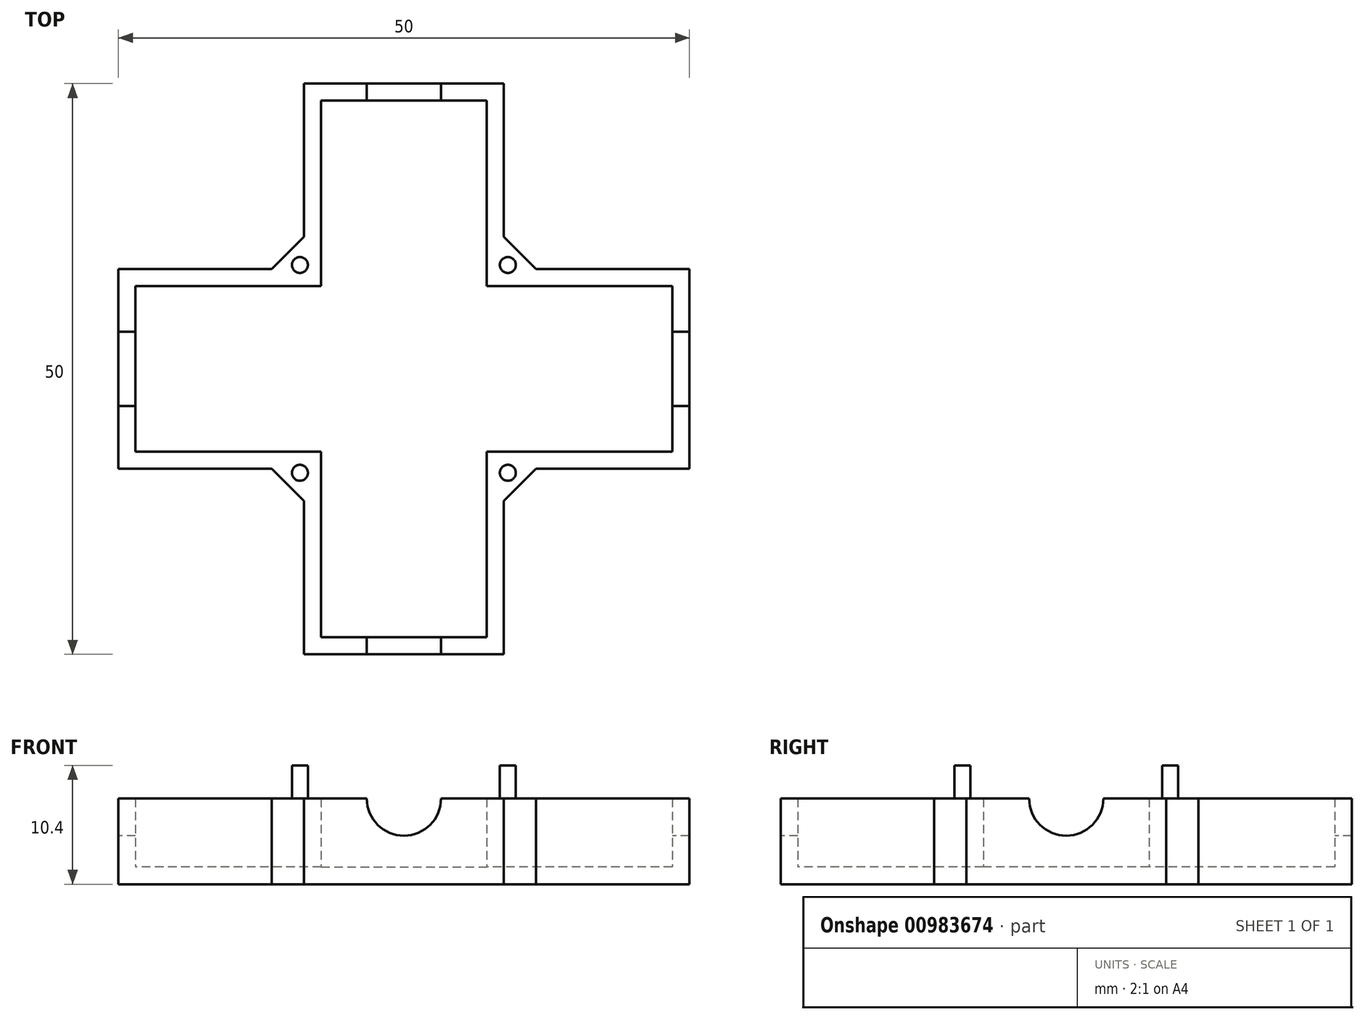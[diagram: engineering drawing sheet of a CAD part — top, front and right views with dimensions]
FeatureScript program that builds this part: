
annotation { "Feature Type Name" : "Feature", "Feature Type Description" : "" }
export const myFeature = defineFeature(function(context is Context, id is Id, definition is map)
    precondition{}
    {
        {
            var Q0;
            Q0=qCreatedBy(makeId("Top.planeOp"),FACE);
            var sketch = newSketch(context, id + "F0", { "sketchPlane" : qUnion([Q0])});
            skLineSegment(sketch, "E0.bottom", {"start": v(25, 8.75) * mm, "end": v(8.75, 8.75) * mm});
            skLineSegment(sketch, "E0.top", {"start": v(25, -8.75) * mm, "end": v(8.75, -8.75) * mm});
            skLineSegment(sketch, "E0.left", {"start": v(25, 8.75) * mm, "end": v(25, -8.75) * mm});
            skLineSegment(sketch, "E0.right", {"start": v(-25, 8.75) * mm, "end": v(-25, -8.75) * mm});
            skPoint(sketch, "E0.middle", {"position": v(0, 0) * mm});
            skLineSegment(sketch, "E1.bottom", {"start": v(-8.75, 25) * mm, "end": v(8.75, 25) * mm});
            skLineSegment(sketch, "E1.top", {"start": v(-8.75, -25) * mm, "end": v(8.75, -25) * mm});
            skLineSegment(sketch, "E1.left", {"start": v(-8.75, 25) * mm, "end": v(-8.75, 8.75) * mm});
            skLineSegment(sketch, "E1.right", {"start": v(8.75, 25) * mm, "end": v(8.75, 8.75) * mm});
            skLineSegment(sketch, "E2.trimOffspring", {"start": v(-8.75, 8.75) * mm, "end": v(-25, 8.75) * mm});
            skLineSegment(sketch, "E3.trimOffspring", {"start": v(-8.75, -8.75) * mm, "end": v(-8.75, -25) * mm});
            skLineSegment(sketch, "E4.trimOffspring", {"start": v(-8.75, -8.75) * mm, "end": v(-25, -8.75) * mm});
            skLineSegment(sketch, "E5.trimOffspring", {"start": v(8.75, -8.75) * mm, "end": v(8.75, -25) * mm});
            skSolve(sketch);
        }
        {
            var Q0;
            Q0=qSketchRegion(id+"F0",true);
            extrude(context, id + "F1", {"entities" : qUnion([Q0]), "depth" : 7.5 * mm, "offsetDistance" : 25 * mm});
        }
        {
            var Q0;
            Q0=makeQuery(id+"F1.opExtrude","CAP_FACE",FACE,{"disambiguationData":[OSD([sQuery(id+"F0.wireOp",EDGE,"E0.bottom"),sQuery(id+"F0.wireOp",EDGE,"E0.top"),sQuery(id+"F0.wireOp",EDGE,"E0.left"),sQuery(id+"F0.wireOp",EDGE,"E0.right"),sQuery(id+"F0.wireOp",EDGE,"E1.bottom"),sQuery(id+"F0.wireOp",EDGE,"E1.top"),sQuery(id+"F0.wireOp",EDGE,"E1.left"),sQuery(id+"F0.wireOp",EDGE,"E1.right"),sQuery(id+"F0.wireOp",EDGE,"E2.trimOffspring"),sQuery(id+"F0.wireOp",EDGE,"E3.trimOffspring"),sQuery(id+"F0.wireOp",EDGE,"E4.trimOffspring"),sQuery(id+"F0.wireOp",EDGE,"E5.trimOffspring")])],"isStart":false});
            shell(context, id + "F2", {"entities" : qUnion([Q0]), "thickness" : 1.5 * mm});
        }
        {
            var Q0;
            Q0=makeQuery(id+"F1.opExtrude","CAP_FACE",FACE,{"disambiguationData":[OSD([sQuery(id+"F0.wireOp",EDGE,"E0.bottom"),sQuery(id+"F0.wireOp",EDGE,"E0.top"),sQuery(id+"F0.wireOp",EDGE,"E0.left"),sQuery(id+"F0.wireOp",EDGE,"E0.right"),sQuery(id+"F0.wireOp",EDGE,"E1.bottom"),sQuery(id+"F0.wireOp",EDGE,"E1.top"),sQuery(id+"F0.wireOp",EDGE,"E1.left"),sQuery(id+"F0.wireOp",EDGE,"E1.right"),sQuery(id+"F0.wireOp",EDGE,"E2.trimOffspring"),sQuery(id+"F0.wireOp",EDGE,"E3.trimOffspring"),sQuery(id+"F0.wireOp",EDGE,"E4.trimOffspring"),sQuery(id+"F0.wireOp",EDGE,"E5.trimOffspring")])],"isStart":false});
            var sketch = newSketch(context, id + "F3", { "sketchPlane" : qUnion([Q0])});
            skLineSegment(sketch, "E6", {"start": v(-11.58, 8.75) * mm, "end": v(-8.75, 11.58) * mm});
            skLineSegment(sketch, "E7", {"start": v(-8.75, 11.58) * mm, "end": v(-8.75, 8.75) * mm});
            skLineSegment(sketch, "E8", {"start": v(-8.75, 8.75) * mm, "end": v(-11.58, 8.75) * mm});
            skLineSegment(sketch, "E9", {"start": v(0, 0) * mm, "end": v(0, 7.25) * mm});
            skLineSegment(sketch, "E10", {"start": v(0, 0) * mm, "end": v(7.25, 0) * mm});
            skLineSegment(sketch, "E11.MirrorCS", {"start": v(8.75, 8.75) * mm, "end": v(11.58, 8.75) * mm});
            skLineSegment(sketch, "E12.MirrorCS", {"start": v(11.58, 8.75) * mm, "end": v(8.75, 11.58) * mm});
            skLineSegment(sketch, "E13.MirrorCS", {"start": v(8.75, 11.58) * mm, "end": v(8.75, 8.75) * mm});
            skLineSegment(sketch, "E14.MirrorCS", {"start": v(-8.75, -8.75) * mm, "end": v(-11.58, -8.75) * mm});
            skLineSegment(sketch, "E15.MirrorCS", {"start": v(8.75, -8.75) * mm, "end": v(11.58, -8.75) * mm});
            skLineSegment(sketch, "E16.MirrorCS", {"start": v(-8.75, -11.58) * mm, "end": v(-8.75, -8.75) * mm});
            skLineSegment(sketch, "E17.MirrorCS", {"start": v(11.58, -8.75) * mm, "end": v(8.75, -11.58) * mm});
            skLineSegment(sketch, "E18.MirrorCS", {"start": v(8.75, -11.58) * mm, "end": v(8.75, -8.75) * mm});
            skLineSegment(sketch, "E19.MirrorCS", {"start": v(-11.58, -8.75) * mm, "end": v(-8.75, -11.58) * mm});
            skSolve(sketch);
        }
        {
            var Q0;
            Q0=qSketchRegion(id+"F3",true);
            var Q1;
            Q1=makeQuery(id+"F1.opExtrude","CAP_FACE",FACE,{"disambiguationData":[OSD([sQuery(id+"F0.wireOp",EDGE,"E0.bottom"),sQuery(id+"F0.wireOp",EDGE,"E0.top"),sQuery(id+"F0.wireOp",EDGE,"E0.left"),sQuery(id+"F0.wireOp",EDGE,"E0.right"),sQuery(id+"F0.wireOp",EDGE,"E1.bottom"),sQuery(id+"F0.wireOp",EDGE,"E1.top"),sQuery(id+"F0.wireOp",EDGE,"E1.left"),sQuery(id+"F0.wireOp",EDGE,"E1.right"),sQuery(id+"F0.wireOp",EDGE,"E2.trimOffspring"),sQuery(id+"F0.wireOp",EDGE,"E3.trimOffspring"),sQuery(id+"F0.wireOp",EDGE,"E4.trimOffspring"),sQuery(id+"F0.wireOp",EDGE,"E5.trimOffspring")])],"isStart":true});
            extrude(context, id + "F4", {"entities" : qUnion([Q0]), "operationType" : NewBodyOperationType.ADD, "endBound" : BoundingType.UP_TO_SURFACE, "oppositeDirection" : true, "depth" : 25 * mm, "endBoundEntityFace" : qUnion([Q1]), "offsetDistance" : 25 * mm});
        }
        {
            var Q0;
            Q0=makeQuery(id+"F4.boolean.opBoolean","MERGE",FACE,{"derivedFrom":[makeQuery(id+"F1.opExtrude","CAP_FACE",FACE,{"disambiguationData":[OSD([sQuery(id+"F0.wireOp",EDGE,"E0.bottom"),sQuery(id+"F0.wireOp",EDGE,"E0.top"),sQuery(id+"F0.wireOp",EDGE,"E0.left"),sQuery(id+"F0.wireOp",EDGE,"E0.right"),sQuery(id+"F0.wireOp",EDGE,"E1.bottom"),sQuery(id+"F0.wireOp",EDGE,"E1.top"),sQuery(id+"F0.wireOp",EDGE,"E1.left"),sQuery(id+"F0.wireOp",EDGE,"E1.right"),sQuery(id+"F0.wireOp",EDGE,"E2.trimOffspring"),sQuery(id+"F0.wireOp",EDGE,"E3.trimOffspring"),sQuery(id+"F0.wireOp",EDGE,"E4.trimOffspring"),sQuery(id+"F0.wireOp",EDGE,"E5.trimOffspring")])],"isStart":false}),makeQuery(id+"F4.opExtrude","CAP_FACE",FACE,{"disambiguationData":[OSD([sQuery(id+"F3.wireOp",EDGE,"E6"),sQuery(id+"F3.wireOp",EDGE,"E7"),sQuery(id+"F3.wireOp",EDGE,"E8")])],"isStart":true}),makeQuery(id+"F4.opExtrude","CAP_FACE",FACE,{"disambiguationData":[OSD([sQuery(id+"F3.wireOp",EDGE,"E11.MirrorCS"),sQuery(id+"F3.wireOp",EDGE,"E12.MirrorCS"),sQuery(id+"F3.wireOp",EDGE,"E13.MirrorCS")])],"isStart":true}),makeQuery(id+"F4.opExtrude","CAP_FACE",FACE,{"disambiguationData":[OSD([sQuery(id+"F3.wireOp",EDGE,"E14.MirrorCS"),sQuery(id+"F3.wireOp",EDGE,"E16.MirrorCS"),sQuery(id+"F3.wireOp",EDGE,"E19.MirrorCS")])],"isStart":true}),makeQuery(id+"F4.opExtrude","CAP_FACE",FACE,{"disambiguationData":[OSD([sQuery(id+"F3.wireOp",EDGE,"E15.MirrorCS"),sQuery(id+"F3.wireOp",EDGE,"E17.MirrorCS"),sQuery(id+"F3.wireOp",EDGE,"E18.MirrorCS")])],"isStart":true})]});
            var sketch = newSketch(context, id + "F5", { "sketchPlane" : qUnion([Q0])});
            skCircle(sketch, "E20", {"center": v(-9.1, 9.1) * mm, "radius": 0.7 * mm});
            skCircle(sketch, "E21", {"center": v(9.1, 9.1) * mm, "radius": 0.7 * mm});
            skCircle(sketch, "E22", {"center": v(9.1, -9.1) * mm, "radius": 0.7 * mm});
            skCircle(sketch, "E23", {"center": v(-9.1, -9.1) * mm, "radius": 0.7 * mm});
            skLineSegment(sketch, "E24", {"start": v(-9.1, 9.1) * mm, "end": v(-10.16, 10.16) * mm});
            skLineSegment(sketch, "E25", {"start": v(9.1, 9.1) * mm, "end": v(10.16, 10.16) * mm});
            skLineSegment(sketch, "E26", {"start": v(9.1, -9.1) * mm, "end": v(10.16, -10.16) * mm});
            skPoint(sketch, "E26.endSnap0", {"position": v(10.16, -10.16) * mm});
            skLineSegment(sketch, "E27", {"start": v(-9.1, -9.1) * mm, "end": v(-10.16, -10.16) * mm});
            skPoint(sketch, "E27.endSnap0", {"position": v(-10.16, -10.16) * mm});
            skSolve(sketch);
        }
        {
            var Q0;
            Q0=qSketchRegion(id+"F5",true);
            extrude(context, id + "F6", {"entities" : qUnion([Q0]), "operationType" : NewBodyOperationType.ADD, "depth" : 2.9 * mm, "offsetDistance" : 25 * mm});
        }
        {
            var Q0;
            Q0=makeQuery(id+"F1.opExtrude","SWEPT_FACE",FACE,{"disambiguationData":[OSD([sQuery(id+"F0.wireOp",EDGE,"E1.top")])]});
            var sketch = newSketch(context, id + "F7", { "sketchPlane" : qUnion([Q0])});
            skCircle(sketch, "E28", {"center": v(0, 7.5) * mm, "radius": 3.25 * mm});
            skSolve(sketch);
        }
        {
            var Q0;
            Q0=qSketchRegion(id+"F7",true);
            extrude(context, id + "F8", {"entities" : qUnion([Q0]), "operationType" : NewBodyOperationType.REMOVE, "endBound" : BoundingType.THROUGH_ALL, "oppositeDirection" : true, "depth" : 25 * mm, "offsetDistance" : 25 * mm});
        }
        {
            var Q0;
            Q0=makeQuery(id+"F1.opExtrude","SWEPT_FACE",FACE,{"disambiguationData":[OSD([sQuery(id+"F0.wireOp",EDGE,"E0.right")])]});
            var sketch = newSketch(context, id + "F9", { "sketchPlane" : qUnion([Q0])});
            skCircle(sketch, "E29", {"center": v(0, 7.5) * mm, "radius": 3.25 * mm});
            skSolve(sketch);
        }
        {
            var Q0;
            Q0=qSketchRegion(id+"F9",true);
            extrude(context, id + "F10", {"entities" : qUnion([Q0]), "operationType" : NewBodyOperationType.REMOVE, "endBound" : BoundingType.THROUGH_ALL, "oppositeDirection" : true, "depth" : 25 * mm, "offsetDistance" : 25 * mm});
        }
    });
